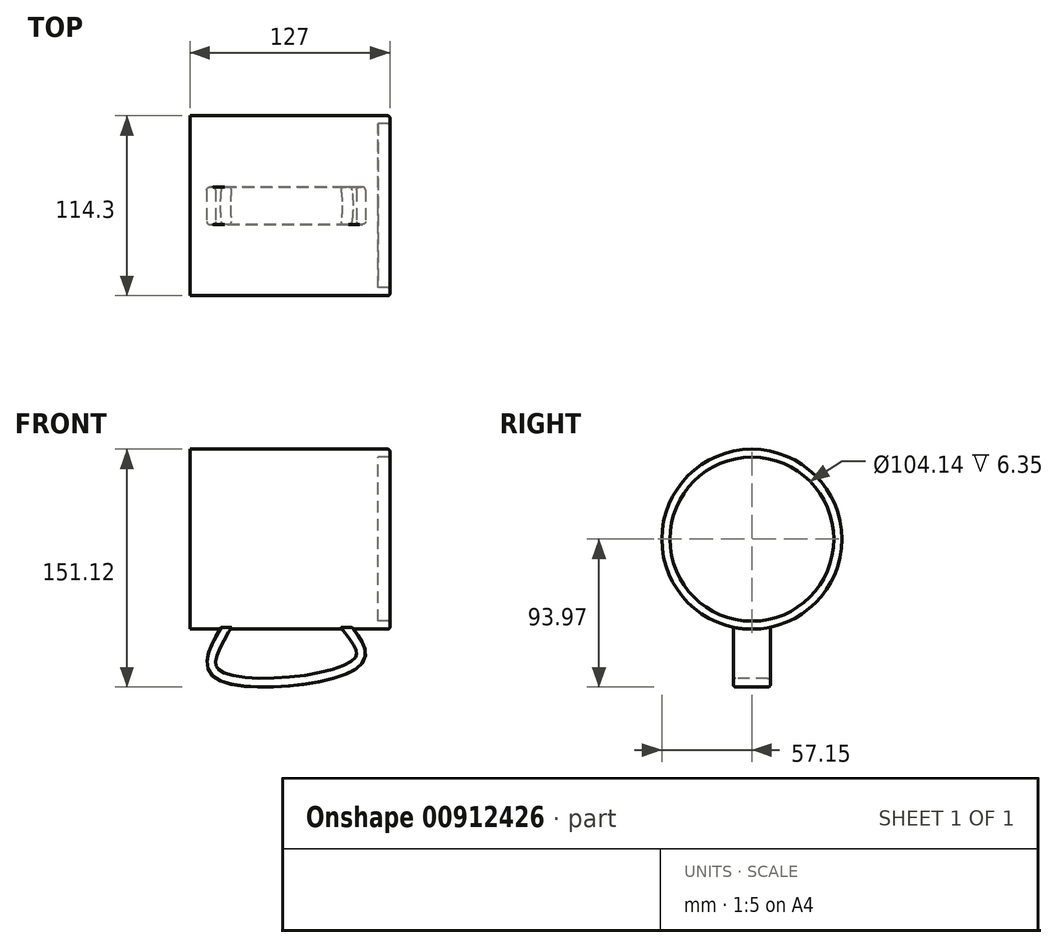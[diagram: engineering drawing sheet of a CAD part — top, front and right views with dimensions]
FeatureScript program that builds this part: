
annotation { "Feature Type Name" : "Feature", "Feature Type Description" : "" }
export const myFeature = defineFeature(function(context is Context, id is Id, definition is map)
    precondition{}
    {
        {
            var Q0;
            Q0=qCreatedBy(makeId("Right.planeOp"),FACE);
            var sketch = newSketch(context, id + "F0", { "sketchPlane" : qUnion([Q0])});
            skCircle(sketch, "E0", {"center": v(0, 0) * mm, "radius": 57.15 * mm});
            skSolve(sketch);
        }
        {
            var Q0;
            Q0=makeQuery(id+"F0.imprint","IMPRINT",FACE,{"disambiguationData":[TD([[makeQuery(id+"F0.imprint","IMPRINT",EDGE,{"derivedFrom":sQuery(id+"F0.wireOp",EDGE,"E0")}),1.0]])]});
            extrude(context, id + "F1", {"entities" : qUnion([Q0]), "depth" : 127 * mm, "offsetDistance" : 25.4 * mm});
        }
        {
            var Q0;
            Q0=makeQuery(id+"F1.opExtrude","CAP_FACE",FACE,{"disambiguationData":[OSD([sQuery(id+"F0.wireOp",EDGE,"E0")])],"isStart":false});
            shell(context, id + "F2", {"entities" : qUnion([Q0]), "thickness" : 5.08 * mm});
        }
        {
            var Q0;
            Q0=qCreatedBy(makeId("Front.planeOp"),FACE);
            var sketch = newSketch(context, id + "F3", { "sketchPlane" : qUnion([Q0])});
            skFitSpline(sketch, "E1", {"points": [v(100.72, -57.7) * mm, v(106.17, -78.28) * mm, v(17.57, -85.76) * mm, v(22.29, -57.6) * mm], "startDerivative": vector(72.34, -92.65) * mm, "endDerivative": vector(71.43, 121.18) * mm});
            skSolve(sketch);
        }
        {
            var Q0;
            Q0=sQuery(id+"F3.wireOp",VERTEX,"E1.start");
            var Q1;
            Q1=sQuery(id+"F3.wireOp",EDGE,"E1");
            cPlane(context, id + "F4", {"entities" : qUnion([Q0, Q1]), "cplaneType" : CPlaneType.CURVE_POINT, "offset" : 25.4 * mm, "width" : 152.4 * mm, "height" : 152.4 * mm});
        }
        {
            var Q0;
            Q0=qCreatedBy(id+"F4.planeOp",FACE);
            var sketch = newSketch(context, id + "F5", { "sketchPlane" : qUnion([Q0])});
            skLineSegment(sketch, "E2.bottom", {"start": v(46.7, 11.8) * mm, "end": v(41.05, 11.8) * mm});
            skLineSegment(sketch, "E2.top", {"start": v(46.7, -11.8) * mm, "end": v(41.05, -11.8) * mm});
            skLineSegment(sketch, "E2.left", {"start": v(46.7, 11.8) * mm, "end": v(46.7, -11.8) * mm});
            skLineSegment(sketch, "E2.right", {"start": v(41.05, 11.8) * mm, "end": v(41.05, -11.8) * mm});
            skPoint(sketch, "E2.middle", {"position": v(43.88, 0) * mm});
            skSolve(sketch);
        }
        {
            var Q0;
            Q0=makeQuery(id+"F5.imprint","IMPRINT",FACE,{"disambiguationData":[TD([[makeQuery(id+"F5.imprint","IMPRINT",EDGE,{"derivedFrom":sQuery(id+"F5.wireOp",EDGE,"E2.bottom")}),1.0]])]});
            var Q1;
            Q1=sQuery(id+"F3.wireOp",EDGE,"E1");
            sweep(context, id + "F6", {"operationType" : NewBodyOperationType.ADD, "profiles" : qUnion([Q0]), "path" : qUnion([Q1])});
        }
        {
            var Q0;
            Q0=makeQuery(id+"F6.opSweep","CAP_FACE",FACE,{"disambiguationData":[OSD([sQuery(id+"F3.wireOp",VERTEX,"E1.start"),sQuery(id+"F5.wireOp",EDGE,"E2.bottom"),sQuery(id+"F5.wireOp",EDGE,"E2.top"),sQuery(id+"F5.wireOp",EDGE,"E2.left"),sQuery(id+"F5.wireOp",EDGE,"E2.right")])],"isStart":true});
            extrude(context, id + "F7", {"entities" : qUnion([Q0]), "operationType" : NewBodyOperationType.ADD, "depth" : 4.57 * mm, "offsetDistance" : 25.4 * mm});
        }
        {
            var Q0;
            Q0=makeQuery(id+"F6.opSweep","CAP_FACE",FACE,{"disambiguationData":[OSD([sQuery(id+"F3.wireOp",VERTEX,"E1.end"),sQuery(id+"F5.wireOp",EDGE,"E2.bottom"),sQuery(id+"F5.wireOp",EDGE,"E2.top"),sQuery(id+"F5.wireOp",EDGE,"E2.left"),sQuery(id+"F5.wireOp",EDGE,"E2.right")])],"isStart":false});
            extrude(context, id + "F8", {"entities" : qUnion([Q0]), "operationType" : NewBodyOperationType.ADD, "depth" : 4.57 * mm, "offsetDistance" : 25.4 * mm});
        }
        {
            var Q0;
            Q0=makeQuery(id+"F6.opSweep","SWEPT_EDGE",EDGE,{"disambiguationData":[OSD([sQuery(id+"F3.wireOp",EDGE,"E1"),sQuery(id+"F5.wireOp",EDGE,"E2.bottom"),sQuery(id+"F5.wireOp",EDGE,"E2.left")])]});
            var Q1;
            Q1=makeQuery(id+"F6.opSweep","SWEPT_EDGE",EDGE,{"disambiguationData":[OSD([sQuery(id+"F3.wireOp",EDGE,"E1"),sQuery(id+"F5.wireOp",EDGE,"E2.bottom"),sQuery(id+"F5.wireOp",EDGE,"E2.right")])]});
            var Q2;
            Q2=makeQuery(id+"F6.opSweep","SWEPT_EDGE",EDGE,{"disambiguationData":[OSD([sQuery(id+"F3.wireOp",EDGE,"E1"),sQuery(id+"F5.wireOp",EDGE,"E2.top"),sQuery(id+"F5.wireOp",EDGE,"E2.left")])]});
            var Q3;
            Q3=makeQuery(id+"F6.opSweep","SWEPT_EDGE",EDGE,{"disambiguationData":[OSD([sQuery(id+"F3.wireOp",EDGE,"E1"),sQuery(id+"F5.wireOp",EDGE,"E2.top"),sQuery(id+"F5.wireOp",EDGE,"E2.right")])]});
            var Q4;
            Q4=makeQuery(id+"F7.opExtrude","SWEPT_EDGE",EDGE,{"disambiguationData":[OSD([sQuery(id+"F3.wireOp",EDGE,"E1"),sQuery(id+"F5.wireOp",EDGE,"E2.top"),sQuery(id+"F5.wireOp",EDGE,"E2.right")])]});
            var Q5;
            Q5=makeQuery(id+"F8.opExtrude","SWEPT_EDGE",EDGE,{"disambiguationData":[OSD([sQuery(id+"F3.wireOp",EDGE,"E1"),sQuery(id+"F5.wireOp",EDGE,"E2.top"),sQuery(id+"F5.wireOp",EDGE,"E2.right")])]});
            var Q6;
            Q6=makeQuery(id+"F8.opExtrude","SWEPT_EDGE",EDGE,{"disambiguationData":[OSD([sQuery(id+"F3.wireOp",EDGE,"E1"),sQuery(id+"F5.wireOp",EDGE,"E2.bottom"),sQuery(id+"F5.wireOp",EDGE,"E2.right")])]});
            var Q7;
            Q7=makeQuery(id+"F7.opExtrude","SWEPT_EDGE",EDGE,{"disambiguationData":[OSD([sQuery(id+"F3.wireOp",EDGE,"E1"),sQuery(id+"F5.wireOp",EDGE,"E2.bottom"),sQuery(id+"F5.wireOp",EDGE,"E2.right")])]});
            fillet(context, id + "F9", {"entities" : qUnion([Q0, Q1, Q2, Q3, Q4, Q5, Q6, Q7]), "radius" : 1.78 * mm, "tangentPropagation" : true, "allowEdgeOverflow" : false});
        }
        {
            var Q0;
            {var subQ0=sQuery(id+"F0.wireOp",EDGE,"E0");Q0=makeQuery(id+"F2.opShell","OFFSET_FACE",FACE,{"disambiguationData":[OSD([subQ0]),TDD([makeQuery(id+"F1.opExtrude","CAP_FACE",FACE,{"disambiguationData":[OSD([subQ0])],"isStart":true})])]});}
            extrude(context, id + "F10", {"entities" : qUnion([Q0]), "operationType" : NewBodyOperationType.ADD, "depth" : 114.3 * mm, "offsetDistance" : 25.4 * mm});
        }
        {
            var Q0;
            Q0=makeQuery(id+"F1.opExtrude","CAP_EDGE",EDGE,{"disambiguationData":[OSD([sQuery(id+"F0.wireOp",EDGE,"E0")])],"isStart":false});
            var Q1;
            {var subQ0=sQuery(id+"F0.wireOp",EDGE,"E0");Q1=makeQuery(id+"F2.opShell","OFFSET_EDGE",EDGE,{"disambiguationData":[OSD([subQ0]),TDD([makeQuery(id+"F1.opExtrude","CAP_EDGE",EDGE,{"disambiguationData":[OSD([subQ0])],"isStart":false})])]});}
            fillet(context, id + "F11", {"entities" : qUnion([Q0, Q1]), "radius" : 1.27 * mm, "tangentPropagation" : true, "allowEdgeOverflow" : false});
        }
    });
